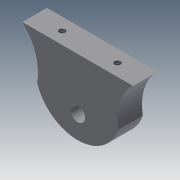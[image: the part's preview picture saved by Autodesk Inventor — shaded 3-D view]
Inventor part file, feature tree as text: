
AUTODESK INVENTOR PART (.ipt)
format: ipt  version: 2013 (Build 170138000, 138)  size: 102,912 bytes
history: native  units: mm
features: sketch x4, extrude x3, hole x1
ambient origin geometry x8: Origin, YZ Plane, XZ Plane, XY Plane, X Axis, Y Axis, Z Axis, Center Point
bodies: Solid1 (feature_tree)
feature tree (8):
  extrude  "Extrusion1"  Depth=6.0mm
  hole  "Hole1"  [1 undecoded]
  extrude  "Extrusion2"  Depth=3.0mm
  extrude  "Extrusion3"  Depth=10.0mm TaperAngle=0.0deg
  sketch  "Sketch1"  dims[d0=45.0mm d4=6.0mm]
  sketch  "Sketch2"  dims[d5=20.0mm d6=20.0mm]
  sketch  "Sketch3"  dims[d7=10.0mm d8=0.0mm d10=3.0mm]
  sketch  "Sketch4"  dims[d11=3.0mm d12=2.459mm d13=5.984mm d14=3.023mm d15=2.0mm d16=14.3117mm d17=8.0mm d18=20.594885mm d19=10.0mm d20=0.0mm d21=21.0mm d22=6.0mm d23=10.0mm d24=0.0mm]
note: 1 required parameter value undecoded (feature->parameter linkage not recoverable at this tier; creation-order binding heuristic only, values carry confidence <= 0.55)
